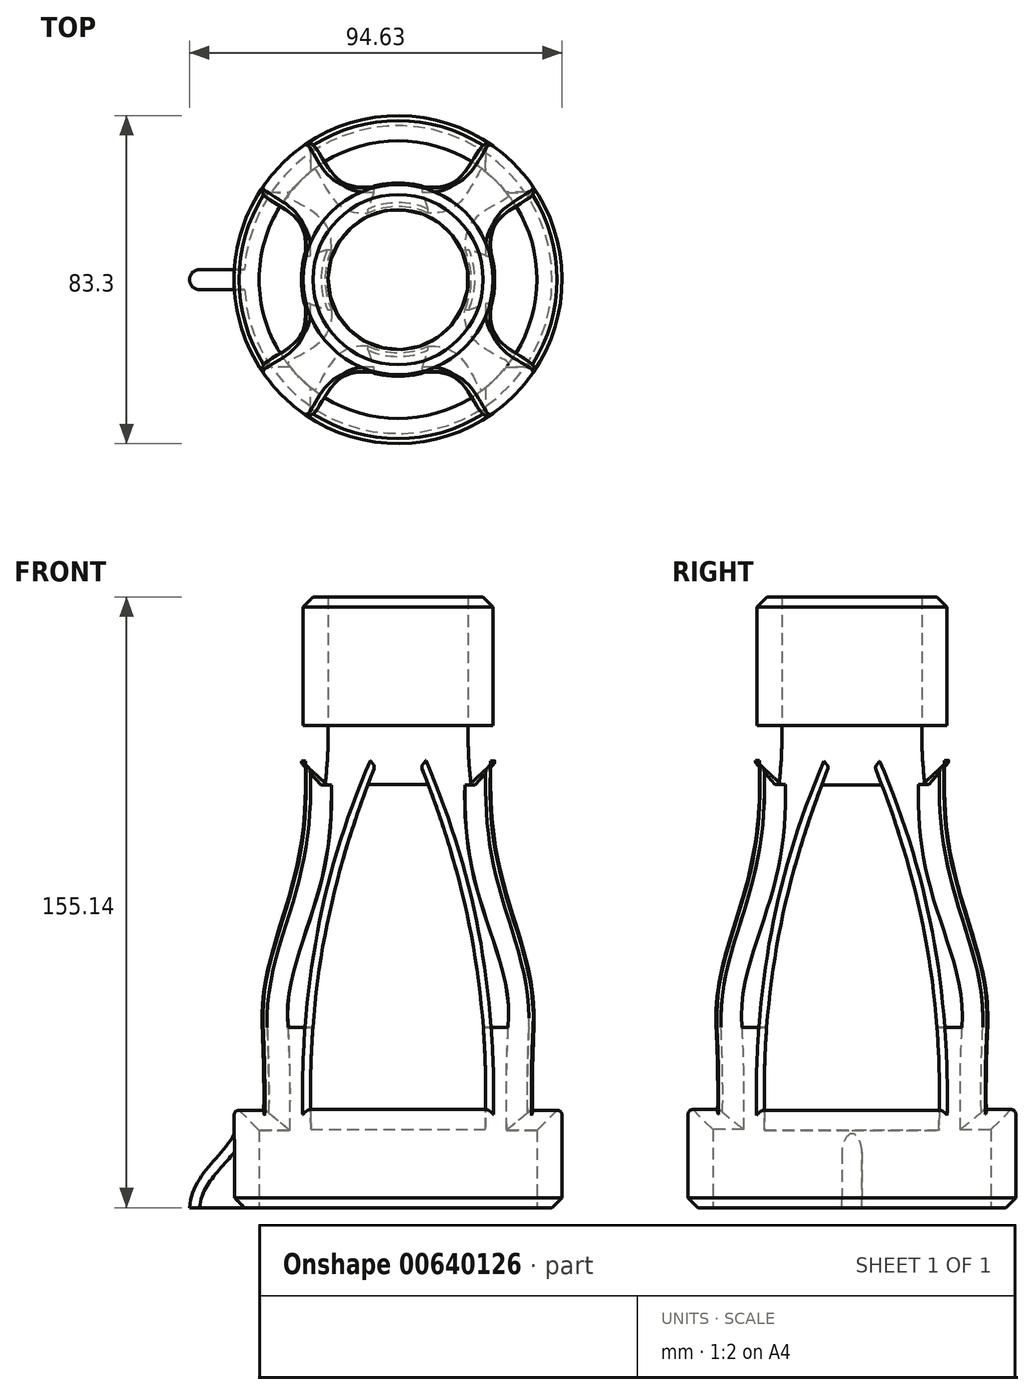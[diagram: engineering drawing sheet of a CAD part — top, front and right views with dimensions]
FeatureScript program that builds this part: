
annotation { "Feature Type Name" : "Feature", "Feature Type Description" : "" }
export const myFeature = defineFeature(function(context is Context, id is Id, definition is map)
    precondition{}
    {
        {
            var Q0;
            Q0=qCreatedBy(makeId("Front.planeOp"),FACE);
            var sketch = newSketch(context, id + "F0", { "sketchPlane" : qUnion([Q0])});
            skLineSegment(sketch, "E0.bottom", {"start": v(0, 0) * mm, "end": v(41.65, 0) * mm});
            skLineSegment(sketch, "E0.top", {"start": v(0, 45.83) * mm, "end": v(41.65, 45.83) * mm});
            skLineSegment(sketch, "E0.left", {"start": v(0, 0) * mm, "end": v(0, 45.83) * mm});
            skLineSegment(sketch, "E0.right", {"start": v(41.65, 0) * mm, "end": v(41.65, 45.83) * mm});
            skLineSegment(sketch, "E1", {"start": v(0, 45.83) * mm, "end": v(0, 122.57) * mm});
            skLineSegment(sketch, "E2.bottom", {"start": v(0, 122.57) * mm, "end": v(24.15, 122.57) * mm});
            skLineSegment(sketch, "E2.top", {"start": v(0, 155.14) * mm, "end": v(24.15, 155.14) * mm});
            skLineSegment(sketch, "E2.left", {"start": v(0, 122.57) * mm, "end": v(0, 155.14) * mm});
            skLineSegment(sketch, "E2.right", {"start": v(24.15, 122.57) * mm, "end": v(24.15, 155.14) * mm});
            skFitSpline(sketch, "E3", {"points": [v(24.15, 122.57) * mm, v(41.65, 45.83) * mm], "startDerivative": vector(0, -107.02) * mm, "endDerivative": vector(0, -71.7) * mm});
            skLineSegment(sketch, "E4.0", {"start": v(17.8, 122.57) * mm, "end": v(17.8, 155.14) * mm});
            skFitSpline(sketch, "E4.1", {"points": [v(17.8, 122.57) * mm, v(17.8, 117.85) * mm, v(18.38, 108.99) * mm, v(20.56, 97.22) * mm, v(23.59, 86.78) * mm, v(26.97, 77.43) * mm, v(30.24, 68.92) * mm, v(32.97, 61.02) * mm, v(34.82, 53.47) * mm, v(35.3, 48.43) * mm, v(35.3, 45.83) * mm]});
            skLineSegment(sketch, "E4.2", {"start": v(35.3, 0) * mm, "end": v(35.3, 45.83) * mm});
            skSolve(sketch);
        }
        {
            var Q0;
            {var subQ0=sQuery(id+"F0.wireOp",EDGE,"E2.right");Q0=makeQuery(id+"F0.imprint","IMPRINT",FACE,{"disambiguationData":[TD([[makeQuery(id+"F0.imprint","IMPRINT",EDGE,{"derivedFrom":subQ0}),1.0]])]});}
            var Q1;
            {var subQ0=sQuery(id+"F0.wireOp",EDGE,"E3");Q1=makeQuery(id+"F0.imprint","IMPRINT",FACE,{"disambiguationData":[TD([[makeQuery(id+"F0.imprint","IMPRINT",EDGE,{"derivedFrom":subQ0}),-1.0]])]});}
            var Q2;
            {var subQ0=sQuery(id+"F0.wireOp",EDGE,"E0.right");Q2=makeQuery(id+"F0.imprint","IMPRINT",FACE,{"disambiguationData":[TD([[makeQuery(id+"F0.imprint","IMPRINT",EDGE,{"derivedFrom":subQ0}),1.0]])]});}
            var Q3;
            Q3=sQuery(id+"F0.wireOp",EDGE,"E1");
            revolve(context, id + "F1", {"entities" : qUnion([Q0, Q1, Q2]), "axis" : qUnion([Q3]), "revolveType" : RevolveType.FULL});
        }
        {
            var Q0;
            Q0=makeQuery(id+"F1.opRevolve","SWEPT_EDGE",EDGE,{"disambiguationData":[OSD([sQuery(id+"F0.wireOp",EDGE,"E2.top"),sQuery(id+"F0.wireOp",EDGE,"E2.right")])]});
            var Q1;
            Q1=makeQuery(id+"F1.opRevolve","SWEPT_EDGE",EDGE,{"disambiguationData":[OSD([sQuery(id+"F0.wireOp",EDGE,"E0.bottom"),sQuery(id+"F0.wireOp",EDGE,"E0.right")])]});
            chamfer(context, id + "F2", {"entities" : qUnion([Q0, Q1]), "width" : 2.54 * mm, "tangentPropagation" : true});
        }
        {
            var Q0;
            Q0=qCreatedBy(makeId("Front.planeOp"),FACE);
            var sketch = newSketch(context, id + "F3", { "sketchPlane" : qUnion([Q0])});
            skLineSegment(sketch, "E5", {"start": v(0, 0) * mm, "end": v(0, 18.2) * mm});
            skLineSegment(sketch, "E6", {"start": v(3.81, 24.92) * mm, "end": v(22.23, 24.92) * mm});
            skLineSegment(sketch, "E7", {"start": v(0, 24.92) * mm, "end": v(0, 107.57) * mm});
            skLineSegment(sketch, "E8", {"start": v(0, 107.57) * mm, "end": v(7.62, 107.57) * mm});
            skLineSegment(sketch, "E9.MirrorCS", {"start": v(0, 107.57) * mm, "end": v(-7.62, 107.57) * mm});
            skLineSegment(sketch, "E10.MirrorCS", {"start": v(-3.8, 24.92) * mm, "end": v(-22.23, 24.92) * mm});
            skPoint(sketch, "E11.orphan", {"position": v(33.02, 24.92) * mm});
            skPoint(sketch, "E12.orphan", {"position": v(-25.4, 24.92) * mm});
            skFitSpline(sketch, "E13", {"points": [v(-7.62, 107.57) * mm, v(-22.23, 24.92) * mm], "startDerivative": vector(-28.03, -73.65) * mm, "endDerivative": vector(1.57, -96.04) * mm});
            skFitSpline(sketch, "E14.MirrorCS", {"points": [v(7.62, 107.57) * mm, v(22.23, 24.92) * mm], "startDerivative": vector(28.03, -73.65) * mm, "endDerivative": vector(-1.57, -96.04) * mm});
            skLineSegment(sketch, "E15", {"start": v(-3.8, 24.92) * mm, "end": v(0, 24.92) * mm});
            skLineSegment(sketch, "E16", {"start": v(3.81, 24.92) * mm, "end": v(0, 24.92) * mm});
            skSolve(sketch);
        }
        {
            var Q0;
            Q0 = qSketchRegion(id + "F3", true);
            extrude(context, id + "F4", {"entities" : qUnion([Q0]), "operationType" : NewBodyOperationType.REMOVE, "depth" : 130.8 * mm, "offsetDistance" : 25.4 * mm, "hasSecondDirection" : true, "secondDirectionOppositeDirection" : true, "secondDirectionDepth" : 93.73 * mm});
        }
        {
            var Q0;
            Q0=qCreatedBy(makeId("Right.planeOp"),FACE);
            var sketch = newSketch(context, id + "F5", { "sketchPlane" : qUnion([Q0])});
            skLineSegment(sketch, "E17", {"start": v(-0.53, 6.56) * mm, "end": v(-0.53, 24.77) * mm});
            skLineSegment(sketch, "E18", {"start": v(-3.84, 24.77) * mm, "end": v(22.2, 24.77) * mm});
            skLineSegment(sketch, "E19", {"start": v(-0.53, 24.77) * mm, "end": v(-0.53, 107.41) * mm});
            skLineSegment(sketch, "E20", {"start": v(-0.53, 107.41) * mm, "end": v(7.6, 107.41) * mm});
            skLineSegment(sketch, "E21.MirrorCS", {"start": v(-0.53, 107.41) * mm, "end": v(-4.34, 107.41) * mm});
            skLineSegment(sketch, "E22.MirrorCS", {"start": v(-0.53, 24.77) * mm, "end": v(-18.95, 24.77) * mm});
            skLineSegment(sketch, "E23", {"start": v(-0.53, -0.16) * mm, "end": v(-0.53, 18.05) * mm});
            skLineSegment(sketch, "E24", {"start": v(7.09, 24.77) * mm, "end": v(25.5, 24.77) * mm});
            skLineSegment(sketch, "E25", {"start": v(-0.03, 24.77) * mm, "end": v(-0.03, 107.41) * mm});
            skLineSegment(sketch, "E26", {"start": v(-0.03, 107.41) * mm, "end": v(7.6, 107.41) * mm});
            skLineSegment(sketch, "E27.MirrorCS", {"start": v(-0.03, 107.41) * mm, "end": v(-7.65, 107.41) * mm});
            skLineSegment(sketch, "E28.MirrorCS", {"start": v(-3.84, 24.77) * mm, "end": v(-22.25, 24.77) * mm});
            skPoint(sketch, "E29.orphan", {"position": v(32.49, 24.77) * mm});
            skPoint(sketch, "E30.orphan", {"position": v(-25.93, 24.77) * mm});
            skFitSpline(sketch, "E31", {"points": [v(-7.65, 107.41) * mm, v(-22.25, 24.77) * mm], "startDerivative": vector(-28.03, -73.65) * mm, "endDerivative": vector(1.57, -96.04) * mm});
            skFitSpline(sketch, "E32.MirrorCS", {"points": [v(7.6, 107.41) * mm, v(22.2, 24.77) * mm], "startDerivative": vector(28.03, -73.65) * mm, "endDerivative": vector(-1.57, -96.04) * mm});
            skPoint(sketch, "E33.orphan", {"position": v(24.87, 24.77) * mm});
            skPoint(sketch, "E34.orphan", {"position": v(-11.96, 107.41) * mm});
            skPoint(sketch, "E35.orphan", {"position": v(10.9, 107.41) * mm});
            skSolve(sketch);
        }
        {
            var Q0;
            Q0 = qSketchRegion(id + "F5", true);
            extrude(context, id + "F6", {"entities" : qUnion([Q0]), "operationType" : NewBodyOperationType.REMOVE, "oppositeDirection" : true, "depth" : 84.07 * mm, "offsetDistance" : 25.4 * mm, "hasSecondDirection" : true, "secondDirectionOppositeDirection" : false, "secondDirectionDepth" : 114.3 * mm});
        }
        {
            var Q0;
            Q0=makeQuery(id+"F4.boolean.opBoolean","INTERSECT",EDGE,{"disambiguationData":[OD(0.0)],"derivedFrom":[makeQuery(id+"F1.opRevolve","SWEPT_FACE",FACE,{"disambiguationData":[OSD([sQuery(id+"F0.wireOp",EDGE,"E4.2")])]}),makeQuery(id+"F4.opExtrude","SWEPT_FACE",FACE,{"disambiguationData":[OSD([sQuery(id+"F3.wireOp",EDGE,"E6"),sQuery(id+"F3.wireOp",EDGE,"E10.MirrorCS"),sQuery(id+"F3.wireOp",EDGE,"E15"),sQuery(id+"F3.wireOp",EDGE,"E16")])]})]});
            var Q1;
            Q1=makeQuery(id+"F4.boolean.opBoolean","INTERSECT",EDGE,{"disambiguationData":[OD(1.0)],"derivedFrom":[makeQuery(id+"F1.opRevolve","SWEPT_FACE",FACE,{"disambiguationData":[OSD([sQuery(id+"F0.wireOp",EDGE,"E4.2")])]}),makeQuery(id+"F4.opExtrude","SWEPT_FACE",FACE,{"disambiguationData":[OSD([sQuery(id+"F3.wireOp",EDGE,"E6"),sQuery(id+"F3.wireOp",EDGE,"E10.MirrorCS"),sQuery(id+"F3.wireOp",EDGE,"E15"),sQuery(id+"F3.wireOp",EDGE,"E16")])]})]});
            var Q2;
            Q2=makeQuery(id+"F6.boolean.opBoolean","INTERSECT",EDGE,{"disambiguationData":[OD(0.0)],"derivedFrom":[makeQuery(id+"F1.opRevolve","SWEPT_FACE",FACE,{"disambiguationData":[OSD([sQuery(id+"F0.wireOp",EDGE,"E4.2")])]}),makeQuery(id+"F6.opExtrude","SWEPT_FACE",FACE,{"disambiguationData":[OSD([sQuery(id+"F5.wireOp",EDGE,"E18"),sQuery(id+"F5.wireOp",EDGE,"E22.MirrorCS"),sQuery(id+"F5.wireOp",EDGE,"E24"),sQuery(id+"F5.wireOp",EDGE,"E28.MirrorCS")])]})]});
            var Q3;
            Q3=makeQuery(id+"F6.boolean.opBoolean","INTERSECT",EDGE,{"disambiguationData":[OD(1.0)],"derivedFrom":[makeQuery(id+"F1.opRevolve","SWEPT_FACE",FACE,{"disambiguationData":[OSD([sQuery(id+"F0.wireOp",EDGE,"E4.2")])]}),makeQuery(id+"F6.opExtrude","SWEPT_FACE",FACE,{"disambiguationData":[OSD([sQuery(id+"F5.wireOp",EDGE,"E18"),sQuery(id+"F5.wireOp",EDGE,"E22.MirrorCS"),sQuery(id+"F5.wireOp",EDGE,"E24"),sQuery(id+"F5.wireOp",EDGE,"E28.MirrorCS")])]})]});
            var Q4;
            Q4=makeQuery(id+"F4.boolean.opBoolean","INTERSECT",EDGE,{"disambiguationData":[OD(0.0)],"derivedFrom":[makeQuery(id+"F1.opRevolve","SWEPT_FACE",FACE,{"disambiguationData":[OSD([sQuery(id+"F0.wireOp",EDGE,"E3")])]}),makeQuery(id+"F4.opExtrude","SWEPT_FACE",FACE,{"disambiguationData":[OSD([sQuery(id+"F3.wireOp",EDGE,"E8"),sQuery(id+"F3.wireOp",EDGE,"E9.MirrorCS")])]})]});
            var Q5;
            Q5=makeQuery(id+"F6.boolean.opBoolean","INTERSECT",EDGE,{"disambiguationData":[OD(0.0)],"derivedFrom":[makeQuery(id+"F1.opRevolve","SWEPT_FACE",FACE,{"disambiguationData":[OSD([sQuery(id+"F0.wireOp",EDGE,"E3")])]}),makeQuery(id+"F6.opExtrude","SWEPT_FACE",FACE,{"disambiguationData":[OSD([sQuery(id+"F5.wireOp",EDGE,"E26"),sQuery(id+"F5.wireOp",EDGE,"E27.MirrorCS")])]})]});
            var Q6;
            Q6=makeQuery(id+"F4.boolean.opBoolean","INTERSECT",EDGE,{"disambiguationData":[OD(1.0)],"derivedFrom":[makeQuery(id+"F1.opRevolve","SWEPT_FACE",FACE,{"disambiguationData":[OSD([sQuery(id+"F0.wireOp",EDGE,"E3")])]}),makeQuery(id+"F4.opExtrude","SWEPT_FACE",FACE,{"disambiguationData":[OSD([sQuery(id+"F3.wireOp",EDGE,"E8"),sQuery(id+"F3.wireOp",EDGE,"E9.MirrorCS")])]})]});
            var Q7;
            Q7=makeQuery(id+"F6.boolean.opBoolean","INTERSECT",EDGE,{"disambiguationData":[OD(1.0)],"derivedFrom":[makeQuery(id+"F1.opRevolve","SWEPT_FACE",FACE,{"disambiguationData":[OSD([sQuery(id+"F0.wireOp",EDGE,"E3")])]}),makeQuery(id+"F6.opExtrude","SWEPT_FACE",FACE,{"disambiguationData":[OSD([sQuery(id+"F5.wireOp",EDGE,"E26"),sQuery(id+"F5.wireOp",EDGE,"E27.MirrorCS")])]})]});
            chamfer(context, id + "F7", {"entities" : qUnion([Q0, Q1, Q2, Q3, Q4, Q5, Q6, Q7]), "width" : 5.08 * mm, "tangentPropagation" : true});
        }
        {
            var Q0;
            Q0=qCreatedBy(makeId("Front.planeOp"),FACE);
            var sketch = newSketch(context, id + "F8", { "sketchPlane" : qUnion([Q0])});
            skLineSegment(sketch, "E36", {"start": v(41.61, 0) * mm, "end": v(53.44, 0) * mm});
            skLineSegment(sketch, "E37", {"start": v(53.44, 0) * mm, "end": v(41.61, 0) * mm});
            skFitSpline(sketch, "E38", {"points": [v(41.15, 21.05) * mm, v(52.98, 0) * mm], "startDerivative": vector(0, -17.89) * mm, "endDerivative": vector(1.4, -28.57) * mm});
            skLineSegment(sketch, "E39", {"start": v(38.31, 0) * mm, "end": v(41.61, 0) * mm});
            skLineSegment(sketch, "E40", {"start": v(41.15, 21.05) * mm, "end": v(38.31, 0) * mm});
            skLineSegment(sketch, "E41", {"start": v(0, 0) * mm, "end": v(0, 15.91) * mm});
            skLineSegment(sketch, "E42.MirrorCS", {"start": v(-38.31, 0) * mm, "end": v(-41.61, 0) * mm});
            skLineSegment(sketch, "E43.MirrorCS", {"start": v(-41.15, 21.05) * mm, "end": v(-38.31, 0) * mm});
            skLineSegment(sketch, "E44.MirrorCS", {"start": v(-53.44, 0) * mm, "end": v(-41.61, 0) * mm});
            skFitSpline(sketch, "E45.MirrorCS", {"points": [v(-41.15, 21.05) * mm, v(-52.98, 0) * mm], "startDerivative": vector(0, -17.89) * mm, "endDerivative": vector(-1.4, -28.57) * mm});
            skSolve(sketch);
        }
        {
            var Q0;
            Q0=makeQuery(id+"F8.imprint","IMPRINT",FACE,{"disambiguationData":[TD([[makeQuery(id+"F8.imprint","IMPRINT",EDGE,{"derivedFrom":sQuery(id+"F8.wireOp",EDGE,"E37")}),-1.0]])]});
            var Q1;
            {var subQ0=sQuery(id+"F8.wireOp",EDGE,"E42.MirrorCS");Q1=makeQuery(id+"F8.imprint","IMPRINT",FACE,{"disambiguationData":[TD([[makeQuery(id+"F8.imprint","IMPRINT",EDGE,{"derivedFrom":subQ0}),-1.0]])]});}
            extrude(context, id + "F9", {"entities" : qUnion([Q0, Q1]), "operationType" : NewBodyOperationType.ADD, "depth" : 2.54 * mm, "offsetDistance" : 25.4 * mm, "hasSecondDirection" : true, "secondDirectionOppositeDirection" : true, "secondDirectionDepth" : 2.54 * mm});
        }
        {
            var Q0;
            Q0=makeQuery(id+"F9.opExtrude","CAP_EDGE",EDGE,{"disambiguationData":[OSD([sQuery(id+"F8.wireOp",EDGE,"E38")])],"isStart":false});
            var Q1;
            Q1=makeQuery(id+"F9.opExtrude","CAP_EDGE",EDGE,{"disambiguationData":[OSD([sQuery(id+"F8.wireOp",EDGE,"E38")])],"isStart":true});
            var Q2;
            Q2=makeQuery(id+"F9.opExtrude","CAP_EDGE",EDGE,{"disambiguationData":[OSD([sQuery(id+"F8.wireOp",EDGE,"E45.MirrorCS")])],"isStart":false});
            var Q3;
            Q3=makeQuery(id+"F9.opExtrude","CAP_EDGE",EDGE,{"disambiguationData":[OSD([sQuery(id+"F8.wireOp",EDGE,"E45.MirrorCS")])],"isStart":true});
            fillet(context, id + "F10", {"entities" : qUnion([Q0, Q1, Q2, Q3]), "radius" : 2.54 * mm, "tangentPropagation" : true, "allowEdgeOverflow" : false});
        }
        {
            var Q0;
            Q0=makeQuery(id+"F4.boolean.opBoolean","INTERSECT",EDGE,{"disambiguationData":[OD(0.0)],"derivedFrom":[makeQuery(id+"F1.opRevolve","SWEPT_FACE",FACE,{"disambiguationData":[OSD([sQuery(id+"F0.wireOp",EDGE,"E0.right")])]}),makeQuery(id+"F4.opExtrude","SWEPT_FACE",FACE,{"disambiguationData":[OSD([sQuery(id+"F3.wireOp",EDGE,"E6"),sQuery(id+"F3.wireOp",EDGE,"E10.MirrorCS"),sQuery(id+"F3.wireOp",EDGE,"E15"),sQuery(id+"F3.wireOp",EDGE,"E16")])]})]});
            var Q1;
            Q1=makeQuery(id+"F6.boolean.opBoolean","INTERSECT",EDGE,{"disambiguationData":[OD(0.0)],"derivedFrom":[makeQuery(id+"F1.opRevolve","SWEPT_FACE",FACE,{"disambiguationData":[OSD([sQuery(id+"F0.wireOp",EDGE,"E0.right")])]}),makeQuery(id+"F6.opExtrude","SWEPT_FACE",FACE,{"disambiguationData":[OSD([sQuery(id+"F5.wireOp",EDGE,"E18"),sQuery(id+"F5.wireOp",EDGE,"E22.MirrorCS"),sQuery(id+"F5.wireOp",EDGE,"E24"),sQuery(id+"F5.wireOp",EDGE,"E28.MirrorCS")])]})]});
            var Q2;
            Q2=makeQuery(id+"F6.boolean.opBoolean","INTERSECT",EDGE,{"disambiguationData":[OD(1.0)],"derivedFrom":[makeQuery(id+"F1.opRevolve","SWEPT_FACE",FACE,{"disambiguationData":[OSD([sQuery(id+"F0.wireOp",EDGE,"E0.right")])]}),makeQuery(id+"F6.opExtrude","SWEPT_FACE",FACE,{"disambiguationData":[OSD([sQuery(id+"F5.wireOp",EDGE,"E18"),sQuery(id+"F5.wireOp",EDGE,"E22.MirrorCS"),sQuery(id+"F5.wireOp",EDGE,"E24"),sQuery(id+"F5.wireOp",EDGE,"E28.MirrorCS")])]})]});
            var Q3;
            Q3=makeQuery(id+"F4.boolean.opBoolean","INTERSECT",EDGE,{"disambiguationData":[OD(1.0)],"derivedFrom":[makeQuery(id+"F1.opRevolve","SWEPT_FACE",FACE,{"disambiguationData":[OSD([sQuery(id+"F0.wireOp",EDGE,"E0.right")])]}),makeQuery(id+"F4.opExtrude","SWEPT_FACE",FACE,{"disambiguationData":[OSD([sQuery(id+"F3.wireOp",EDGE,"E6"),sQuery(id+"F3.wireOp",EDGE,"E10.MirrorCS"),sQuery(id+"F3.wireOp",EDGE,"E15"),sQuery(id+"F3.wireOp",EDGE,"E16")])]})]});
            fillet(context, id + "F11", {"entities" : qUnion([Q0, Q1, Q2, Q3]), "radius" : 1.27 * mm, "tangentPropagation" : true, "allowEdgeOverflow" : false});
        }
        {
            var Q0;
            Q0=makeQuery(id+"F4.boolean.opBoolean","INTERSECT",EDGE,{"disambiguationData":[OD(0.0)],"derivedFrom":[makeQuery(id+"F1.opRevolve","SWEPT_FACE",FACE,{"disambiguationData":[OSD([sQuery(id+"F0.wireOp",EDGE,"E3")])]}),makeQuery(id+"F4.opExtrude","SWEPT_FACE",FACE,{"disambiguationData":[OSD([sQuery(id+"F3.wireOp",EDGE,"E14.MirrorCS")])]})]});
            var Q1;
            Q1=makeQuery(id+"F4.boolean.opBoolean","INTERSECT",EDGE,{"disambiguationData":[OD(0.0)],"derivedFrom":[makeQuery(id+"F1.opRevolve","SWEPT_FACE",FACE,{"disambiguationData":[OSD([sQuery(id+"F0.wireOp",EDGE,"E3")])]}),makeQuery(id+"F4.opExtrude","SWEPT_FACE",FACE,{"disambiguationData":[OSD([sQuery(id+"F3.wireOp",EDGE,"E13")])]})]});
            var Q2;
            Q2=makeQuery(id+"F6.boolean.opBoolean","INTERSECT",EDGE,{"disambiguationData":[OD(0.0)],"derivedFrom":[makeQuery(id+"F1.opRevolve","SWEPT_FACE",FACE,{"disambiguationData":[OSD([sQuery(id+"F0.wireOp",EDGE,"E3")])]}),makeQuery(id+"F6.opExtrude","SWEPT_FACE",FACE,{"disambiguationData":[OSD([sQuery(id+"F5.wireOp",EDGE,"E31")])]})]});
            var Q3;
            Q3=makeQuery(id+"F6.boolean.opBoolean","INTERSECT",EDGE,{"disambiguationData":[OD(0.0)],"derivedFrom":[makeQuery(id+"F1.opRevolve","SWEPT_FACE",FACE,{"disambiguationData":[OSD([sQuery(id+"F0.wireOp",EDGE,"E3")])]}),makeQuery(id+"F6.opExtrude","SWEPT_FACE",FACE,{"disambiguationData":[OSD([sQuery(id+"F5.wireOp",EDGE,"E32.MirrorCS")])]})]});
            var Q4;
            Q4=makeQuery(id+"F6.boolean.opBoolean","INTERSECT",EDGE,{"disambiguationData":[OD(1.0)],"derivedFrom":[makeQuery(id+"F1.opRevolve","SWEPT_FACE",FACE,{"disambiguationData":[OSD([sQuery(id+"F0.wireOp",EDGE,"E3")])]}),makeQuery(id+"F6.opExtrude","SWEPT_FACE",FACE,{"disambiguationData":[OSD([sQuery(id+"F5.wireOp",EDGE,"E31")])]})]});
            var Q5;
            Q5=makeQuery(id+"F6.boolean.opBoolean","INTERSECT",EDGE,{"disambiguationData":[OD(1.0)],"derivedFrom":[makeQuery(id+"F1.opRevolve","SWEPT_FACE",FACE,{"disambiguationData":[OSD([sQuery(id+"F0.wireOp",EDGE,"E3")])]}),makeQuery(id+"F6.opExtrude","SWEPT_FACE",FACE,{"disambiguationData":[OSD([sQuery(id+"F5.wireOp",EDGE,"E32.MirrorCS")])]})]});
            var Q6;
            Q6=makeQuery(id+"F4.boolean.opBoolean","INTERSECT",EDGE,{"disambiguationData":[OD(1.0)],"derivedFrom":[makeQuery(id+"F1.opRevolve","SWEPT_FACE",FACE,{"disambiguationData":[OSD([sQuery(id+"F0.wireOp",EDGE,"E3")])]}),makeQuery(id+"F4.opExtrude","SWEPT_FACE",FACE,{"disambiguationData":[OSD([sQuery(id+"F3.wireOp",EDGE,"E13")])]})]});
            var Q7;
            Q7=makeQuery(id+"F4.boolean.opBoolean","INTERSECT",EDGE,{"disambiguationData":[OD(1.0)],"derivedFrom":[makeQuery(id+"F1.opRevolve","SWEPT_FACE",FACE,{"disambiguationData":[OSD([sQuery(id+"F0.wireOp",EDGE,"E3")])]}),makeQuery(id+"F4.opExtrude","SWEPT_FACE",FACE,{"disambiguationData":[OSD([sQuery(id+"F3.wireOp",EDGE,"E14.MirrorCS")])]})]});
            var Q8;
            {var subQ0=makeQuery(id+"F1.opRevolve","SWEPT_FACE",FACE,{"disambiguationData":[OSD([sQuery(id+"F0.wireOp",EDGE,"E3")])]});Q8=makeQuery(id+"F7.opChamfer","BLEND_EDGE",EDGE,{"blendedFrom":[makeQuery(id+"F4.boolean.opBoolean","INTERSECT",EDGE,{"disambiguationData":[OD(1.0)],"derivedFrom":[subQ0,makeQuery(id+"F4.opExtrude","SWEPT_FACE",FACE,{"disambiguationData":[OSD([sQuery(id+"F3.wireOp",EDGE,"E8"),sQuery(id+"F3.wireOp",EDGE,"E9.MirrorCS")])]})]}),subQ0],"blendedInto":[subQ0]});}
            var Q9;
            {var subQ0=makeQuery(id+"F1.opRevolve","SWEPT_FACE",FACE,{"disambiguationData":[OSD([sQuery(id+"F0.wireOp",EDGE,"E3")])]});Q9=makeQuery(id+"F7.opChamfer","BLEND_EDGE",EDGE,{"blendedFrom":[makeQuery(id+"F6.boolean.opBoolean","INTERSECT",EDGE,{"disambiguationData":[OD(0.0)],"derivedFrom":[subQ0,makeQuery(id+"F6.opExtrude","SWEPT_FACE",FACE,{"disambiguationData":[OSD([sQuery(id+"F5.wireOp",EDGE,"E26"),sQuery(id+"F5.wireOp",EDGE,"E27.MirrorCS")])]})]}),subQ0],"blendedInto":[subQ0]});}
            var Q10;
            {var subQ0=makeQuery(id+"F1.opRevolve","SWEPT_FACE",FACE,{"disambiguationData":[OSD([sQuery(id+"F0.wireOp",EDGE,"E3")])]});Q10=makeQuery(id+"F7.opChamfer","BLEND_EDGE",EDGE,{"blendedFrom":[makeQuery(id+"F6.boolean.opBoolean","INTERSECT",EDGE,{"disambiguationData":[OD(1.0)],"derivedFrom":[subQ0,makeQuery(id+"F6.opExtrude","SWEPT_FACE",FACE,{"disambiguationData":[OSD([sQuery(id+"F5.wireOp",EDGE,"E26"),sQuery(id+"F5.wireOp",EDGE,"E27.MirrorCS")])]})]}),subQ0],"blendedInto":[subQ0]});}
            var Q11;
            {var subQ0=makeQuery(id+"F1.opRevolve","SWEPT_FACE",FACE,{"disambiguationData":[OSD([sQuery(id+"F0.wireOp",EDGE,"E3")])]});Q11=makeQuery(id+"F7.opChamfer","BLEND_EDGE",EDGE,{"blendedFrom":[makeQuery(id+"F4.boolean.opBoolean","INTERSECT",EDGE,{"disambiguationData":[OD(0.0)],"derivedFrom":[subQ0,makeQuery(id+"F4.opExtrude","SWEPT_FACE",FACE,{"disambiguationData":[OSD([sQuery(id+"F3.wireOp",EDGE,"E8"),sQuery(id+"F3.wireOp",EDGE,"E9.MirrorCS")])]})]}),subQ0],"blendedInto":[subQ0]});}
            fillet(context, id + "F12", {"entities" : qUnion([Q0, Q1, Q2, Q3, Q4, Q5, Q6, Q7, Q8, Q9, Q10, Q11]), "radius" : 1.27 * mm, "tangentPropagation" : true, "allowEdgeOverflow" : false});
        }
    });
